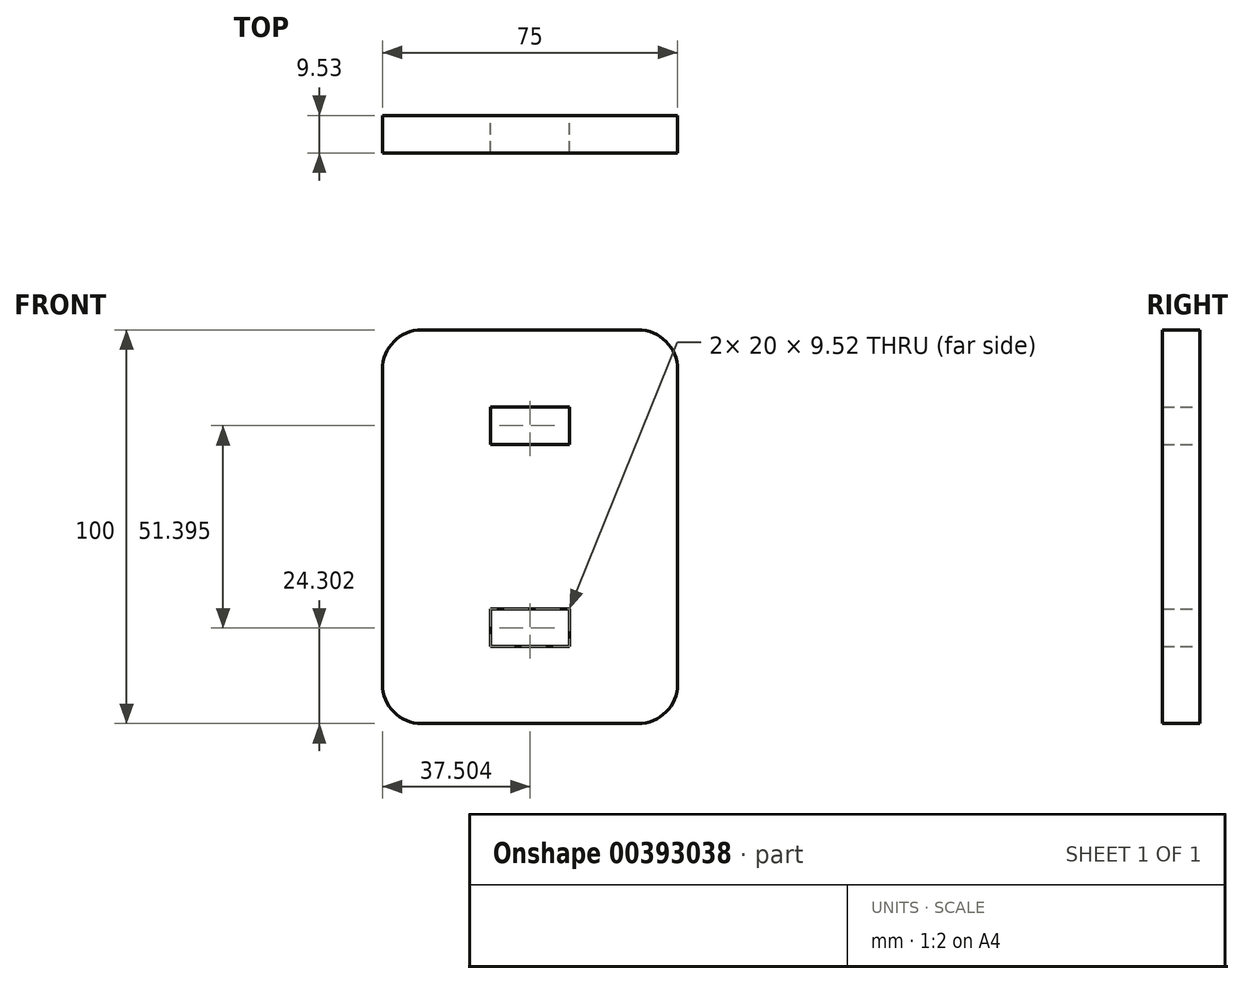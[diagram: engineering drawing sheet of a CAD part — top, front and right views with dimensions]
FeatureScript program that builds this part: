
annotation { "Feature Type Name" : "Feature", "Feature Type Description" : "" }
export const myFeature = defineFeature(function(context is Context, id is Id, definition is map)
    precondition{}
    {
        {
            var Q0;
            Q0=qCreatedBy(makeId("Front.planeOp"),FACE);
            var sketch = newSketch(context, id + "F0", { "sketchPlane" : qUnion([Q0])});
            skLineSegment(sketch, "E0.bottom", {"start": v(-41.5, 61.44) * mm, "end": v(13.5, 61.44) * mm});
            skLineSegment(sketch, "E0.top", {"start": v(-41.5, -38.56) * mm, "end": v(13.5, -38.56) * mm});
            skLineSegment(sketch, "E0.left", {"start": v(-51.5, 51.44) * mm, "end": v(-51.5, -28.56) * mm});
            skLineSegment(sketch, "E0.right", {"start": v(23.5, 51.44) * mm, "end": v(23.5, -28.56) * mm});
            skLineSegment(sketch, "E1", {"start": v(-14, 61.44) * mm, "end": v(-14, -38.56) * mm, "construction": true});
            skLineSegment(sketch, "E2", {"start": v(-14, 41.9) * mm, "end": v(-4, 41.9) * mm});
            skLineSegment(sketch, "E3", {"start": v(-4, 41.9) * mm, "end": v(-4, 32.37) * mm});
            skLineSegment(sketch, "E4", {"start": v(-4, 32.37) * mm, "end": v(-24, 32.37) * mm});
            skLineSegment(sketch, "E5", {"start": v(-24, 32.37) * mm, "end": v(-24, 41.9) * mm});
            skLineSegment(sketch, "E6", {"start": v(-24, 41.9) * mm, "end": v(-14, 41.9) * mm});
            skLineSegment(sketch, "E7", {"start": v(-51.5, 11.44) * mm, "end": v(23.5, 11.44) * mm, "construction": true});
            skLineSegment(sketch, "E8.MirrorCS", {"start": v(-4, -9.5) * mm, "end": v(-24, -9.5) * mm});
            skLineSegment(sketch, "E9.MirrorCS", {"start": v(-14, -19.02) * mm, "end": v(-4, -19.02) * mm});
            skLineSegment(sketch, "E10.MirrorCS", {"start": v(-4, -19.02) * mm, "end": v(-4, -9.5) * mm});
            skLineSegment(sketch, "E11.MirrorCS", {"start": v(-24, -9.5) * mm, "end": v(-24, -19.02) * mm});
            skLineSegment(sketch, "E12.MirrorCS", {"start": v(-24, -19.02) * mm, "end": v(-14, -19.02) * mm});
            skPoint(sketch, "E13.visualSharp", {"position": v(-51.5, 61.44) * mm});
            skArc(sketch, "E13.filletArc", {"start": v(-41.5, 61.44) * mm, "mid": v(-48.57, 58.51) * mm, "end": v(-51.5, 51.44) * mm});
            skPoint(sketch, "E14.visualSharp", {"position": v(23.5, 61.44) * mm});
            skArc(sketch, "E14.filletArc", {"start": v(23.5, 51.44) * mm, "mid": v(20.58, 58.51) * mm, "end": v(13.5, 61.44) * mm});
            skPoint(sketch, "E15.visualSharp", {"position": v(-51.5, -38.56) * mm});
            skArc(sketch, "E15.filletArc", {"start": v(-51.5, -28.56) * mm, "mid": v(-48.57, -35.63) * mm, "end": v(-41.5, -38.56) * mm});
            skPoint(sketch, "E16.visualSharp", {"position": v(23.5, -38.56) * mm});
            skArc(sketch, "E16.filletArc", {"start": v(13.5, -38.56) * mm, "mid": v(20.58, -35.63) * mm, "end": v(23.5, -28.56) * mm});
            skSolve(sketch);
        }
        {
            var Q0;
            Q0 = qSketchRegion(id + "F0", true);
            extrude(context, id + "F1", {"entities" : qUnion([Q0]), "depth" : 9.53 * mm});
        }
    });
